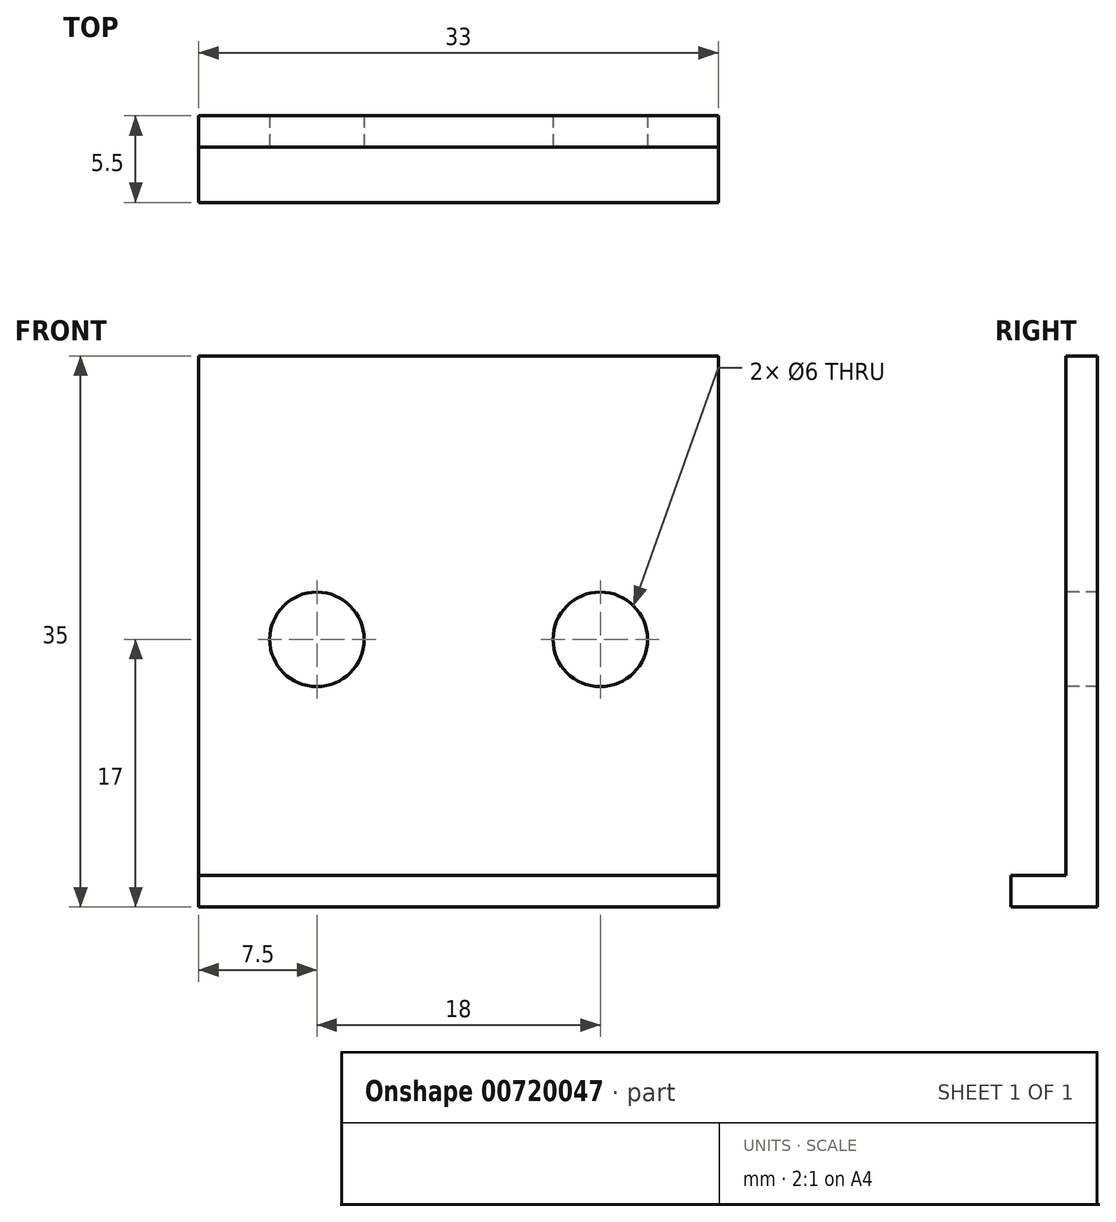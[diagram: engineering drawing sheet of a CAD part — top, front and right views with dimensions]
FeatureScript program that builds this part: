
annotation { "Feature Type Name" : "Feature", "Feature Type Description" : "" }
export const myFeature = defineFeature(function(context is Context, id is Id, definition is map)
    precondition{}
    {
        {
            var Q0;
            Q0=qCreatedBy(makeId("Top.planeOp"),FACE);
            var sketch = newSketch(context, id + "F0", { "sketchPlane" : qUnion([Q0])});
            skLineSegment(sketch, "E0.bottom", {"start": v(16.5, 2.75) * mm, "end": v(-16.5, 2.75) * mm});
            skLineSegment(sketch, "E0.top", {"start": v(16.5, -2.75) * mm, "end": v(-16.5, -2.75) * mm});
            skLineSegment(sketch, "E0.left", {"start": v(16.5, 2.75) * mm, "end": v(16.5, -2.75) * mm});
            skLineSegment(sketch, "E0.right", {"start": v(-16.5, 2.75) * mm, "end": v(-16.5, -2.75) * mm});
            skPoint(sketch, "E0.middle", {"position": v(0, 0) * mm});
            skSolve(sketch);
        }
        {
            var Q0;
            Q0 = qSketchRegion(id + "F0", true);
            extrude(context, id + "F1", {"entities" : qUnion([Q0]), "depth" : 2 * mm, "offsetDistance" : 25 * mm});
        }
        {
            var Q0;
            Q0=makeQuery(id+"F1.opExtrude","CAP_FACE",FACE,{"disambiguationData":[OSD([sQuery(id+"F0.wireOp",EDGE,"E0.bottom"),sQuery(id+"F0.wireOp",EDGE,"E0.top"),sQuery(id+"F0.wireOp",EDGE,"E0.left"),sQuery(id+"F0.wireOp",EDGE,"E0.right")])],"isStart":false});
            var sketch = newSketch(context, id + "F2", { "sketchPlane" : qUnion([Q0])});
            skLineSegment(sketch, "E1.bottom", {"start": v(-16.5, 2.75) * mm, "end": v(16.5, 2.75) * mm});
            skLineSegment(sketch, "E1.top", {"start": v(-16.5, 0.75) * mm, "end": v(16.5, 0.75) * mm});
            skLineSegment(sketch, "E1.left", {"start": v(-16.5, 2.75) * mm, "end": v(-16.5, 0.75) * mm});
            skLineSegment(sketch, "E1.right", {"start": v(16.5, 2.75) * mm, "end": v(16.5, 0.75) * mm});
            skSolve(sketch);
        }
        {
            var Q0;
            Q0 = qSketchRegion(id + "F2", true);
            extrude(context, id + "F3", {"entities" : qUnion([Q0]), "operationType" : NewBodyOperationType.ADD, "depth" : 33 * mm, "offsetDistance" : 25 * mm});
        }
        {
            var Q0;
            Q0=makeQuery(id+"F3.opExtrude","SWEPT_FACE",FACE,{"disambiguationData":[OSD([sQuery(id+"F2.wireOp",EDGE,"E1.top")])]});
            var sketch = newSketch(context, id + "F4", { "sketchPlane" : qUnion([Q0])});
            skCircle(sketch, "E2", {"center": v(-9, 17) * mm, "radius": 3 * mm});
            skCircle(sketch, "E3", {"center": v(9, 17) * mm, "radius": 3 * mm});
            skSolve(sketch);
        }
        {
            var Q0;
            Q0 = qSketchRegion(id + "F4", true);
            extrude(context, id + "F5", {"entities" : qUnion([Q0]), "operationType" : NewBodyOperationType.REMOVE, "endBound" : BoundingType.THROUGH_ALL, "oppositeDirection" : true, "depth" : 25 * mm, "offsetDistance" : 25 * mm});
        }
    });
